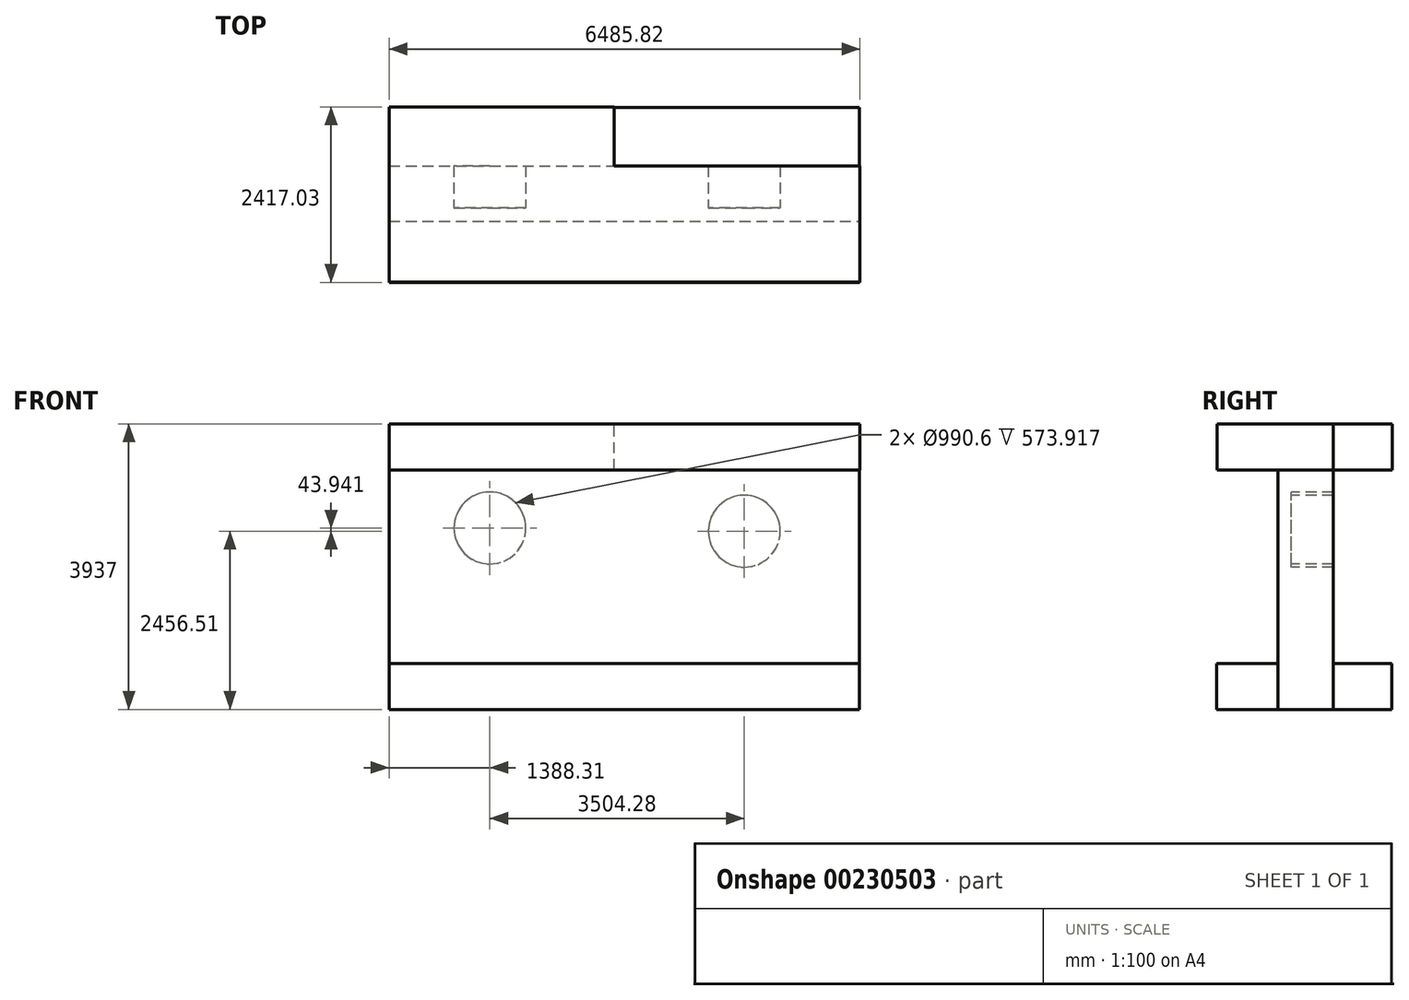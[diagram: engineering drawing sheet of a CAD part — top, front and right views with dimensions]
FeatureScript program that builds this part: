
annotation { "Feature Type Name" : "Feature", "Feature Type Description" : "" }
export const myFeature = defineFeature(function(context is Context, id is Id, definition is map)
    precondition{}
    {
        {
            var Q0;
            Q0=qCreatedBy(makeId("Top.planeOp"),FACE);
            var sketch = newSketch(context, id + "F0", { "sketchPlane" : qUnion([Q0])});
            skLineSegment(sketch, "E0.bottom", {"start": v(-3233.07, 1384.3) * mm, "end": v(3243.93, 1384.3) * mm});
            skLineSegment(sketch, "E0.top", {"start": v(-3233.07, -1028.7) * mm, "end": v(3243.93, -1028.7) * mm});
            skLineSegment(sketch, "E0.left", {"start": v(-3233.07, 1384.3) * mm, "end": v(-3233.07, -1028.7) * mm});
            skLineSegment(sketch, "E0.right", {"start": v(3243.93, 1384.3) * mm, "end": v(3243.93, -1028.7) * mm});
            skLineSegment(sketch, "E1.bottom", {"start": v(-3233.07, 573.92) * mm, "end": v(3243.93, 573.92) * mm});
            skLineSegment(sketch, "E1.top", {"start": v(-3233.07, -186.2) * mm, "end": v(3243.93, -186.2) * mm});
            skLineSegment(sketch, "E1.left", {"start": v(-3233.07, 573.92) * mm, "end": v(-3233.07, -186.2) * mm});
            skLineSegment(sketch, "E1.right", {"start": v(3243.93, 573.92) * mm, "end": v(3243.93, -186.2) * mm});
            skSolve(sketch);
        }
        {
            var Q0;
            {var subQ0=sQuery(id+"F0.wireOp",EDGE,"E0.bottom");Q0=makeQuery(id+"F0.imprint","IMPRINT",FACE,{"disambiguationData":[TD([[makeQuery(id+"F0.imprint","IMPRINT",EDGE,{"derivedFrom":subQ0}),-1.0]])]});}
            var Q1;
            {var subQ0=sQuery(id+"F0.wireOp",EDGE,"E0.top");Q1=makeQuery(id+"F0.imprint","IMPRINT",FACE,{"disambiguationData":[TD([[makeQuery(id+"F0.imprint","IMPRINT",EDGE,{"derivedFrom":subQ0}),1.0]])]});}
            extrude(context, id + "F1", {"entities" : qUnion([Q0, Q1]), "depth" : 635 * mm});
        }
        {
            var Q0;
            Q0=makeQuery(id+"F0.imprint","IMPRINT",FACE,{"disambiguationData":[TD([[makeQuery(id+"F0.imprint","IMPRINT",EDGE,{"derivedFrom":sQuery(id+"F0.wireOp",EDGE,"E1.bottom")}),-1.0]])]});
            extrude(context, id + "F2", {"entities" : qUnion([Q0]), "depth" : 3937 * mm});
        }
        {
            var Q0;
            Q0=qCreatedBy(makeId("Front.planeOp"),FACE);
            var sketch = newSketch(context, id + "F3", { "sketchPlane" : qUnion([Q0])});
            skCircle(sketch, "E2", {"center": v(-1844.76, 2500.45) * mm, "radius": 482.6 * mm});
            skCircle(sketch, "E3", {"center": v(1659.52, 2456.5) * mm, "radius": 482.6 * mm});
            skSolve(sketch);
        }
        {
            var Q0;
            Q0=sQuery(id+"F3.wireOp",VERTEX,"E2.center");
            var Q1;
            Q1=sQuery(id+"F3.wireOp",VERTEX,"E3.center");
            var Q2;
            Q2=makeQuery(id+"F2.opExtrude","SWEPT_BODY",BODY,{"disambiguationData":[OSD([sQuery(id+"F0.wireOp",EDGE,"E1.bottom"),sQuery(id+"F0.wireOp",EDGE,"E1.top"),sQuery(id+"F0.wireOp",EDGE,"E1.left"),sQuery(id+"F0.wireOp",EDGE,"E1.right")])]});
            hole(context, id + "F4", {"style" : HoleStyle.SIMPLE, "endStyle" : HoleEndStyle.THROUGH, "holeDiameter" : 990.6 * mm, "locations" : qUnion([Q0, Q1]), "scope" : qUnion([Q2]), "isTappedThrough" : true});
        }
        {
            var Q0;
            Q0=makeQuery(id+"F2.opExtrude","CAP_FACE",FACE,{"disambiguationData":[OSD([sQuery(id+"F0.wireOp",EDGE,"E1.bottom"),sQuery(id+"F0.wireOp",EDGE,"E1.top"),sQuery(id+"F0.wireOp",EDGE,"E1.left"),sQuery(id+"F0.wireOp",EDGE,"E1.right")])],"isStart":false});
            var sketch = newSketch(context, id + "F5", { "sketchPlane" : qUnion([Q0])});
            skLineSegment(sketch, "E4.bottom", {"start": v(3252.75, 573.92) * mm, "end": v(-3233.07, 573.92) * mm});
            skLineSegment(sketch, "E4.top", {"start": v(3252.75, -1026.33) * mm, "end": v(-3233.07, -1026.33) * mm});
            skLineSegment(sketch, "E4.left", {"start": v(3252.75, 573.92) * mm, "end": v(3252.75, -1026.33) * mm});
            skLineSegment(sketch, "E4.right", {"start": v(-3233.07, 573.92) * mm, "end": v(-3233.07, -1026.33) * mm});
            skLineSegment(sketch, "E5.bottom", {"start": v(-3233.07, -186.2) * mm, "end": v(-134.8, -186.2) * mm});
            skLineSegment(sketch, "E5.top", {"start": v(-3233.07, 1388.32) * mm, "end": v(-134.8, 1388.32) * mm});
            skLineSegment(sketch, "E5.left", {"start": v(-3233.07, -186.2) * mm, "end": v(-3233.07, 1388.32) * mm});
            skLineSegment(sketch, "E5.right", {"start": v(-134.8, -186.2) * mm, "end": v(-134.8, 1388.32) * mm});
            skSolve(sketch);
        }
        {
            var Q0;
            Q0 = qSketchRegion(id + "F5", true);
            extrude(context, id + "F6", {"entities" : qUnion([Q0]), "operationType" : NewBodyOperationType.ADD, "oppositeDirection" : true, "depth" : 635 * mm});
        }
    });
